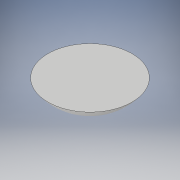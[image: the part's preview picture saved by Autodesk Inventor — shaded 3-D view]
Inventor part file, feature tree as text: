
AUTODESK INVENTOR PART (.ipt)
format: ipt  version: 2019.4 (Build 234330000, 330)  size: 114,176 bytes
history: native  units: mm
features: other x1, revolve x1, sketch x1
ambient origin geometry x8: Origin, YZ Plane, XZ Plane, XY Plane, X Axis, Y Axis, Z Axis, Center Point
bodies: Body1 (feature_tree)
feature tree (3):
  other  "Sólido1"
  revolve  "Revolución1"  [1 undecoded]
  sketch  "Boceto1"  dims[d1=1500.0mm d2=3000.0mm d3=90.0deg]
note: 1 required parameter value undecoded (feature->parameter linkage not recoverable at this tier; creation-order binding heuristic only, values carry confidence <= 0.55)
